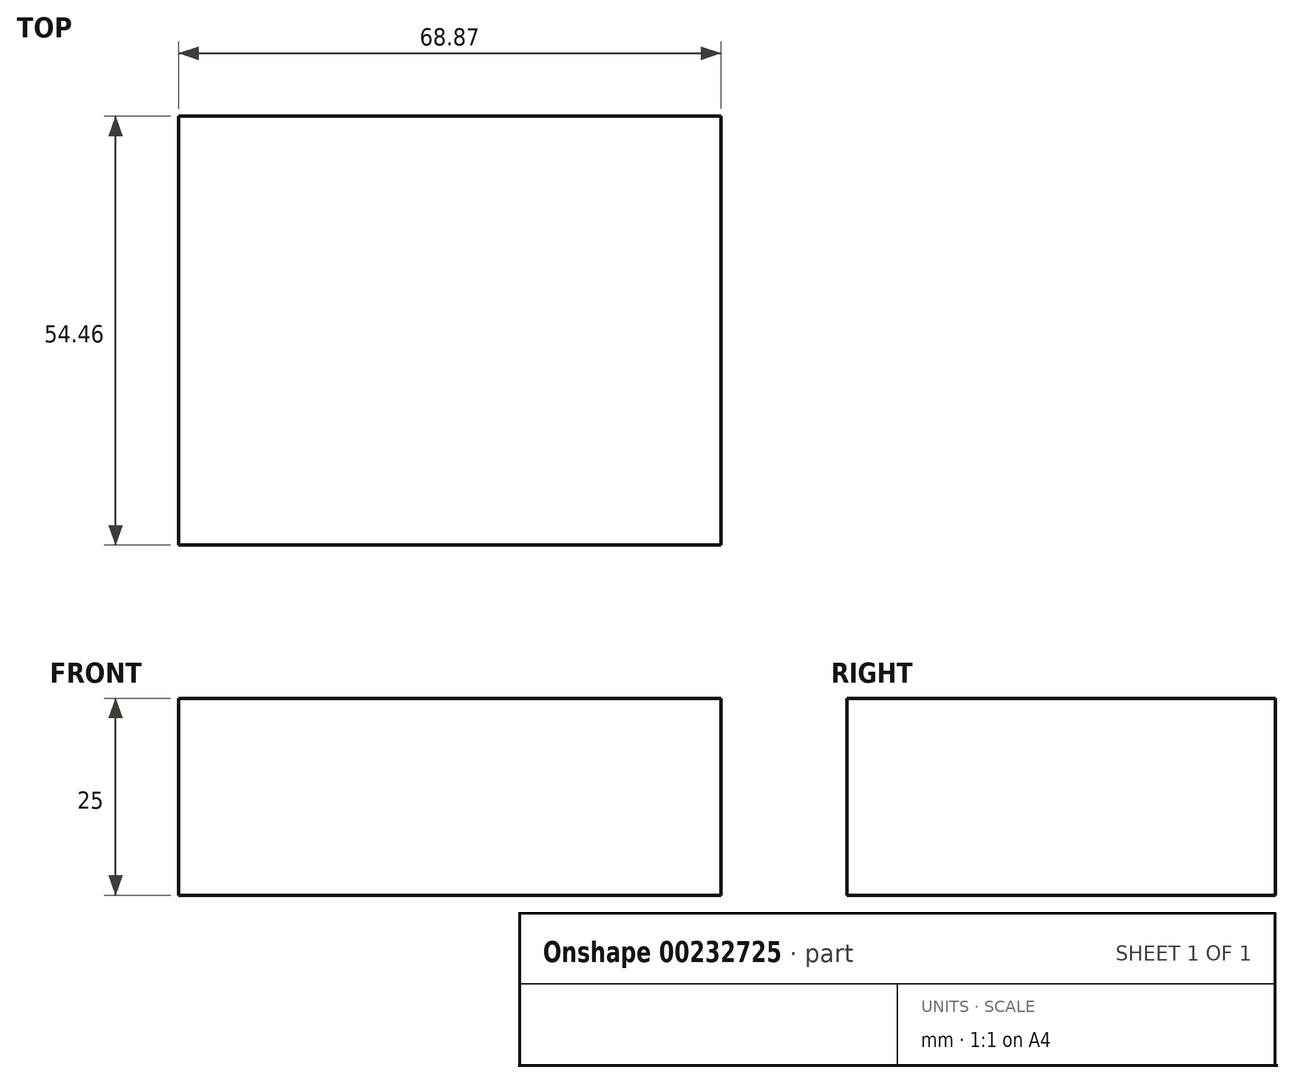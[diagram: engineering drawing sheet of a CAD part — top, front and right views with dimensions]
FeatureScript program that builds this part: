
annotation { "Feature Type Name" : "Feature", "Feature Type Description" : "" }
export const myFeature = defineFeature(function(context is Context, id is Id, definition is map)
    precondition{}
    {
        {
            var Q0;
            Q0=qCreatedBy(makeId("Top.planeOp"),FACE);
            var sketch = newSketch(context, id + "F0", { "sketchPlane" : qUnion([Q0])});
            skLineSegment(sketch, "E0.bottom", {"start": v(-140.41, -40.73) * mm, "end": v(-71.54, -40.73) * mm});
            skLineSegment(sketch, "E0.top", {"start": v(-140.41, -95.2) * mm, "end": v(-71.54, -95.2) * mm});
            skLineSegment(sketch, "E0.left", {"start": v(-140.41, -40.73) * mm, "end": v(-140.41, -95.2) * mm});
            skLineSegment(sketch, "E0.right", {"start": v(-71.54, -40.73) * mm, "end": v(-71.54, -95.2) * mm});
            skSolve(sketch);
        }
        {
            var Q0;
            Q0 = qSketchRegion(id + "F0", true);
            extrude(context, id + "F1", {"entities" : qUnion([Q0]), "depth" : 25 * mm});
        }
    });
